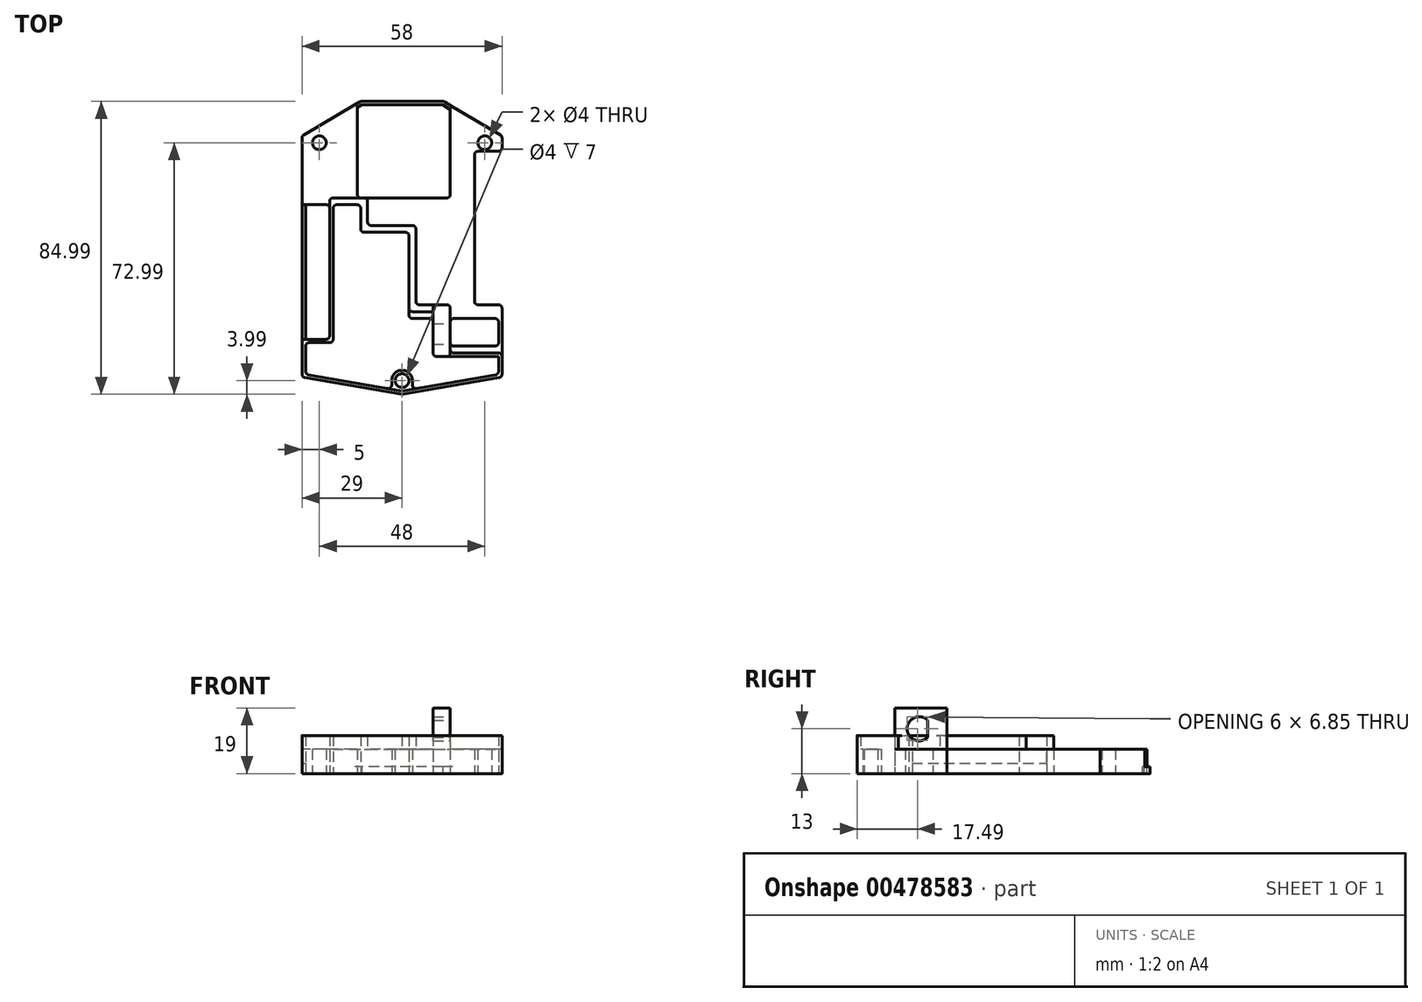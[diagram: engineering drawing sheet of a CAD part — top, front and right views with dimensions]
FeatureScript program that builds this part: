
annotation { "Feature Type Name" : "Feature", "Feature Type Description" : "" }
export const myFeature = defineFeature(function(context is Context, id is Id, definition is map)
    precondition{}
    {
        {
            var Q0;
            Q0=qCreatedBy(makeId("Top.planeOp"),FACE);
            var sketch = newSketch(context, id + "F0", { "sketchPlane" : qUnion([Q0])});
            skCircle(sketch, "E0", {"center": v(0, 0) * mm, "radius": 2 * mm});
            skLineSegment(sketch, "E1", {"start": v(0, 0) * mm, "end": v(0, -4) * mm, "construction": true});
            skLineSegment(sketch, "E2", {"start": v(0, -4) * mm, "end": v(-29, 1) * mm});
            skLineSegment(sketch, "E3.MirrorCS", {"start": v(0, -4) * mm, "end": v(29, 1) * mm});
            skLineSegment(sketch, "E4", {"start": v(-29, 1) * mm, "end": v(29, 1) * mm, "construction": true});
            skLineSegment(sketch, "E5", {"start": v(-29, 1) * mm, "end": v(-29, 71) * mm});
            skLineSegment(sketch, "E6", {"start": v(0, 0) * mm, "end": v(0, 81) * mm, "construction": true});
            skLineSegment(sketch, "E7.MirrorCS", {"start": v(29, 1) * mm, "end": v(29, 71) * mm});
            skLineSegment(sketch, "E8", {"start": v(12, 81) * mm, "end": v(-12, 81) * mm});
            skLineSegment(sketch, "E9", {"start": v(12, 81) * mm, "end": v(29, 71) * mm});
            skLineSegment(sketch, "E10", {"start": v(-12, 81) * mm, "end": v(-29, 71) * mm});
            skCircle(sketch, "E11", {"center": v(24, 69) * mm, "radius": 2 * mm});
            skCircle(sketch, "E12.MirrorC", {"center": v(-24, 69) * mm, "radius": 2 * mm});
            skSolve(sketch);
        }
        {
            var Q0;
            Q0=qCreatedBy(makeId("Top.planeOp"),FACE);
            var sketch = newSketch(context, id + "F1", { "sketchPlane" : qUnion([Q0])});
            skLineSegment(sketch, "E13.0.0", {"start": v(29, 71) * mm, "end": v(12, 81) * mm});
            skLineSegment(sketch, "E13.0.1", {"start": v(12, 81) * mm, "end": v(-12, 81) * mm});
            skLineSegment(sketch, "E13.0.2", {"start": v(-12, 81) * mm, "end": v(-29, 71) * mm});
            skLineSegment(sketch, "E13.0.3", {"start": v(-29, 71) * mm, "end": v(-29, 1) * mm});
            skLineSegment(sketch, "E13.0.4", {"start": v(-29, 1) * mm, "end": v(0, -4) * mm});
            skLineSegment(sketch, "E13.0.5", {"start": v(0, -4) * mm, "end": v(29, 1) * mm});
            skLineSegment(sketch, "E13.0.6", {"start": v(29, 1) * mm, "end": v(29, 22) * mm});
            skCircle(sketch, "E14.0", {"center": v(24, 69) * mm, "radius": 2 * mm});
            skCircle(sketch, "E15.0", {"center": v(-24, 69) * mm, "radius": 2 * mm});
            skCircle(sketch, "E16.0", {"center": v(0, 0) * mm, "radius": 2 * mm});
            skLineSegment(sketch, "E17", {"start": v(28, 18) * mm, "end": v(28, 1.84) * mm});
            skLineSegment(sketch, "E18", {"start": v(28, 1.84) * mm, "end": v(3, -2.47) * mm});
            skLineSegment(sketch, "E19", {"start": v(-3, -2.47) * mm, "end": v(-28, 1.84) * mm});
            skLineSegment(sketch, "E20", {"start": v(-28, 1.84) * mm, "end": v(-28, 51) * mm});
            skLineSegment(sketch, "E21", {"start": v(29, 22) * mm, "end": v(21, 22) * mm});
            skLineSegment(sketch, "E22", {"start": v(21, 22) * mm, "end": v(21, 66.5) * mm});
            skLineSegment(sketch, "E23", {"start": v(21, 66.5) * mm, "end": v(29, 66.5) * mm});
            skLineSegment(sketch, "E24", {"start": v(28, 18) * mm, "end": v(2, 18) * mm});
            skLineSegment(sketch, "E25", {"start": v(2, 18) * mm, "end": v(2, 43) * mm});
            skLineSegment(sketch, "E26", {"start": v(-12, 51) * mm, "end": v(-28, 51) * mm});
            skLineSegment(sketch, "E27", {"start": v(-12, 51) * mm, "end": v(-12, 43) * mm});
            skLineSegment(sketch, "E28", {"start": v(-12, 43) * mm, "end": v(2, 43) * mm});
            skArc(sketch, "E29", {"start": v(3, 0) * mm, "mid": v(0, 3) * mm, "end": v(-3, 0) * mm});
            skLineSegment(sketch, "E30", {"start": v(-3, 0) * mm, "end": v(-3, -2.47) * mm});
            skLineSegment(sketch, "E31", {"start": v(3, 0) * mm, "end": v(3, -2.47) * mm});
            skPoint(sketch, "E32", {"position": v(-28, 51) * mm});
            skPoint(sketch, "E33", {"position": v(28, 18) * mm});
            skPoint(sketch, "E34", {"position": v(28, 22) * mm});
            skPoint(sketch, "E35", {"position": v(28, 66.5) * mm});
            skPoint(sketch, "E36.orphan", {"position": v(-29, 51) * mm});
            skLineSegment(sketch, "E37.trimOffspring", {"start": v(29, 66.5) * mm, "end": v(29, 71) * mm});
            skPoint(sketch, "E38.orphan", {"position": v(0, -2.99) * mm});
            skLineSegment(sketch, "E39", {"start": v(-29, 11) * mm, "end": v(-20, 11) * mm});
            skLineSegment(sketch, "E40", {"start": v(-20, 11) * mm, "end": v(-20, 51) * mm});
            skLineSegment(sketch, "E41", {"start": v(-29, 12) * mm, "end": v(-21, 12) * mm});
            skLineSegment(sketch, "E42", {"start": v(-21, 12) * mm, "end": v(-21, 51) * mm});
            skLineSegment(sketch, "E43", {"start": v(-13, 80.41) * mm, "end": v(-13, 53) * mm});
            skLineSegment(sketch, "E44", {"start": v(-13, 53) * mm, "end": v(14, 53) * mm});
            skLineSegment(sketch, "E45", {"start": v(14, 53) * mm, "end": v(14, 79.82) * mm});
            skLineSegment(sketch, "E46", {"start": v(0, 81) * mm, "end": v(0, 53) * mm, "construction": true});
            skLineSegment(sketch, "E47", {"start": v(14, 78.66) * mm, "end": v(11.73, 80) * mm});
            skLineSegment(sketch, "E48", {"start": v(11.73, 80) * mm, "end": v(-11.73, 80) * mm});
            skLineSegment(sketch, "E49", {"start": v(-11.73, 80) * mm, "end": v(-13, 79.25) * mm});
            skLineSegment(sketch, "E50", {"start": v(28, 10) * mm, "end": v(14, 10) * mm});
            skLineSegment(sketch, "E51", {"start": v(14, 10) * mm, "end": v(14, 18) * mm});
            skLineSegment(sketch, "E52", {"start": v(9, 18) * mm, "end": v(9, 7) * mm});
            skLineSegment(sketch, "E53", {"start": v(9, 7) * mm, "end": v(28, 7) * mm});
            skSolve(sketch);
        }
        {
            var Q0;
            {var subQ0=sQuery(id+"F1.wireOp",EDGE,"E39");var subQ1=sQuery(id+"F1.wireOp",EDGE,"E13.0.3");var subQ2=makeQuery(id+"F1.imprint","INTERSECT",VERTEX,{"derivedFrom":[subQ1,subQ0]});Q0=makeQuery(id+"F1.imprint","IMPRINT",FACE,{"disambiguationData":[TD([[makeQuery(id+"F1.imprint","IMPRINT",EDGE,{"disambiguationData":[TD([[subQ2,1.0]])],"derivedFrom":subQ1}),1.0]])]});}
            var Q1;
            {var subQ0=sQuery(id+"F1.wireOp",EDGE,"E40");Q1=makeQuery(id+"F1.imprint","IMPRINT",FACE,{"disambiguationData":[TD([[makeQuery(id+"F1.imprint","IMPRINT",EDGE,{"derivedFrom":subQ0}),1.0]])]});}
            var Q2;
            {var subQ11=sQuery(id+"F1.wireOp",EDGE,"E13.0.4");Q2=makeQuery(id+"F1.imprint","IMPRINT",FACE,{"disambiguationData":[TD([[makeQuery(id+"F1.imprint","IMPRINT",EDGE,{"derivedFrom":subQ11}),1.0]])]});}
            var Q3;
            {var subQ1=sQuery(id+"F1.wireOp",EDGE,"E50");Q3=makeQuery(id+"F1.imprint","IMPRINT",FACE,{"disambiguationData":[TD([[makeQuery(id+"F1.imprint","IMPRINT",EDGE,{"derivedFrom":subQ1}),1.0]])]});}
            extrude(context, id + "F2", {"entities" : qUnion([Q0, Q1, Q2, Q3]), "depth" : 7 * mm, "offsetDistance" : 25 * mm});
        }
        {
            var Q0;
            Q0=makeQuery(id+"F2.opExtrude","CAP_FACE",FACE,{"disambiguationData":[OSD([sQuery(id+"F1.wireOp",EDGE,"E13.0.0"),sQuery(id+"F1.wireOp",EDGE,"E13.0.1"),sQuery(id+"F1.wireOp",EDGE,"E13.0.2"),sQuery(id+"F1.wireOp",EDGE,"E13.0.3"),sQuery(id+"F1.wireOp",EDGE,"E13.0.4"),sQuery(id+"F1.wireOp",EDGE,"E13.0.5"),sQuery(id+"F1.wireOp",EDGE,"E13.0.6"),sQuery(id+"F1.wireOp",EDGE,"E14.0"),sQuery(id+"F1.wireOp",EDGE,"E15.0"),sQuery(id+"F1.wireOp",EDGE,"E16.0"),sQuery(id+"F1.wireOp",EDGE,"E17"),sQuery(id+"F1.wireOp",EDGE,"E18"),sQuery(id+"F1.wireOp",EDGE,"E19"),sQuery(id+"F1.wireOp",EDGE,"E20"),sQuery(id+"F1.wireOp",EDGE,"E21"),sQuery(id+"F1.wireOp",EDGE,"E22"),sQuery(id+"F1.wireOp",EDGE,"E23"),sQuery(id+"F1.wireOp",EDGE,"E24"),sQuery(id+"F1.wireOp",EDGE,"E25"),sQuery(id+"F1.wireOp",EDGE,"E26"),sQuery(id+"F1.wireOp",EDGE,"E27"),sQuery(id+"F1.wireOp",EDGE,"E28"),sQuery(id+"F1.wireOp",EDGE,"E29"),sQuery(id+"F1.wireOp",EDGE,"E30"),sQuery(id+"F1.wireOp",EDGE,"E31"),sQuery(id+"F1.wireOp",EDGE,"E37.trimOffspring"),sQuery(id+"F1.wireOp",EDGE,"E39"),sQuery(id+"F1.wireOp",EDGE,"E40"),sQuery(id+"F1.wireOp",EDGE,"E41"),sQuery(id+"F1.wireOp",EDGE,"E42")])],"isStart":false});
            var sketch = newSketch(context, id + "F3", { "sketchPlane" : qUnion([Q0])});
            skLineSegment(sketch, "E54", {"start": v(21, 22) * mm, "end": v(21, 33) * mm});
            skLineSegment(sketch, "E55", {"start": v(4, 33) * mm, "end": v(4, 45) * mm});
            skLineSegment(sketch, "E56", {"start": v(4, 45) * mm, "end": v(-10, 45) * mm});
            skLineSegment(sketch, "E57", {"start": v(-10, 45) * mm, "end": v(-10, 53) * mm});
            skLineSegment(sketch, "E58", {"start": v(-10, 53) * mm, "end": v(-21, 53) * mm});
            skLineSegment(sketch, "E59", {"start": v(-21, 53) * mm, "end": v(-21, 51) * mm});
            skLineSegment(sketch, "E60.0", {"start": v(-21, 12) * mm, "end": v(-21, 51) * mm});
            skLineSegment(sketch, "E61.0", {"start": v(-28, 12) * mm, "end": v(-21, 12) * mm});
            skLineSegment(sketch, "E62.0", {"start": v(-28, 11) * mm, "end": v(-20, 11) * mm});
            skLineSegment(sketch, "E63.0", {"start": v(-20, 11) * mm, "end": v(-20, 51) * mm});
            skLineSegment(sketch, "E64", {"start": v(-20, 51) * mm, "end": v(-12, 51) * mm});
            skLineSegment(sketch, "E65.0", {"start": v(-12, 51) * mm, "end": v(-12, 43) * mm});
            skLineSegment(sketch, "E66.0", {"start": v(-12, 43) * mm, "end": v(2, 43) * mm});
            skLineSegment(sketch, "E67", {"start": v(2, 33) * mm, "end": v(2, 43) * mm});
            skLineSegment(sketch, "E68", {"start": v(-28, 12) * mm, "end": v(-29, 12) * mm});
            skLineSegment(sketch, "E69", {"start": v(-29, 12) * mm, "end": v(-29, 1) * mm});
            skLineSegment(sketch, "E70", {"start": v(-29, 1) * mm, "end": v(-3.17, -3.45) * mm});
            skLineSegment(sketch, "E71", {"start": v(-3.17, -3.45) * mm, "end": v(-3, -2.47) * mm});
            skLineSegment(sketch, "E72", {"start": v(-3, -2.47) * mm, "end": v(-28, 1.84) * mm});
            skLineSegment(sketch, "E73", {"start": v(-28, 1.84) * mm, "end": v(-28, 11) * mm});
            skLineSegment(sketch, "E74.0", {"start": v(29, 22) * mm, "end": v(21, 22) * mm});
            skLineSegment(sketch, "E75.0", {"start": v(28, 1.84) * mm, "end": v(3, -2.47) * mm});
            skLineSegment(sketch, "E76.0", {"start": v(-29, 1) * mm, "end": v(0, -4) * mm});
            skLineSegment(sketch, "E77.0", {"start": v(0, -4) * mm, "end": v(29, 1) * mm});
            skLineSegment(sketch, "E78.0", {"start": v(29, 1) * mm, "end": v(29, 8) * mm});
            skLineSegment(sketch, "E79", {"start": v(-3, -2.47) * mm, "end": v(0, -2.99) * mm});
            skLineSegment(sketch, "E80", {"start": v(0, -2.99) * mm, "end": v(3, -2.47) * mm});
            skLineSegment(sketch, "E81", {"start": v(2, 31) * mm, "end": v(2, 33) * mm});
            skLineSegment(sketch, "E82", {"start": v(9, 20) * mm, "end": v(2, 20) * mm});
            skLineSegment(sketch, "E83", {"start": v(2, 20) * mm, "end": v(2, 31) * mm});
            skLineSegment(sketch, "E84", {"start": v(4, 33) * mm, "end": v(4, 22) * mm});
            skLineSegment(sketch, "E85", {"start": v(4, 22) * mm, "end": v(21, 22) * mm});
            skLineSegment(sketch, "E86.0", {"start": v(9, 18) * mm, "end": v(9, 7) * mm});
            skLineSegment(sketch, "E87.0", {"start": v(14, 10) * mm, "end": v(14, 18) * mm});
            skLineSegment(sketch, "E88", {"start": v(9, 18) * mm, "end": v(9, 20) * mm});
            skLineSegment(sketch, "E89", {"start": v(14, 18) * mm, "end": v(14, 20) * mm});
            skLineSegment(sketch, "E90", {"start": v(14, 10) * mm, "end": v(14, 8) * mm});
            skLineSegment(sketch, "E91", {"start": v(14, 8) * mm, "end": v(29, 8) * mm});
            skLineSegment(sketch, "E92.0", {"start": v(9, 7) * mm, "end": v(28, 7) * mm});
            skLineSegment(sketch, "E93.0", {"start": v(28, 7) * mm, "end": v(28, 1.84) * mm});
            skLineSegment(sketch, "E94", {"start": v(14, 20) * mm, "end": v(14, 22) * mm});
            skSolve(sketch);
        }
        {
            var Q0;
            Q0 = qSketchRegion(id + "F3", true);
            extrude(context, id + "F4", {"entities" : qUnion([Q0]), "operationType" : NewBodyOperationType.ADD, "depth" : 4 * mm, "offsetDistance" : 25 * mm});
        }
        {
            var Q0;
            Q0=makeQuery(id+"F4.opExtrude","CAP_FACE",FACE,{"disambiguationData":[OSD([sQuery(id+"F3.wireOp",EDGE,"E55"),sQuery(id+"F3.wireOp",EDGE,"E56"),sQuery(id+"F3.wireOp",EDGE,"E57"),sQuery(id+"F3.wireOp",EDGE,"E58"),sQuery(id+"F3.wireOp",EDGE,"E59"),sQuery(id+"F3.wireOp",EDGE,"E60.0"),sQuery(id+"F3.wireOp",EDGE,"E61.0"),sQuery(id+"F3.wireOp",EDGE,"E62.0"),sQuery(id+"F3.wireOp",EDGE,"E63.0"),sQuery(id+"F3.wireOp",EDGE,"E64"),sQuery(id+"F3.wireOp",EDGE,"E65.0"),sQuery(id+"F3.wireOp",EDGE,"E66.0"),sQuery(id+"F3.wireOp",EDGE,"E67"),sQuery(id+"F3.wireOp",EDGE,"E68"),sQuery(id+"F3.wireOp",EDGE,"E69"),sQuery(id+"F3.wireOp",EDGE,"E72"),sQuery(id+"F3.wireOp",EDGE,"E73"),sQuery(id+"F3.wireOp",EDGE,"E75.0"),sQuery(id+"F3.wireOp",EDGE,"E76.0"),sQuery(id+"F3.wireOp",EDGE,"E77.0"),sQuery(id+"F3.wireOp",EDGE,"E78.0"),sQuery(id+"F3.wireOp",EDGE,"E79"),sQuery(id+"F3.wireOp",EDGE,"E80"),sQuery(id+"F3.wireOp",EDGE,"E81"),sQuery(id+"F3.wireOp",EDGE,"E82"),sQuery(id+"F3.wireOp",EDGE,"E83"),sQuery(id+"F3.wireOp",EDGE,"E84"),sQuery(id+"F3.wireOp",EDGE,"E85"),sQuery(id+"F3.wireOp",EDGE,"E86.0"),sQuery(id+"F3.wireOp",EDGE,"E87.0"),sQuery(id+"F3.wireOp",EDGE,"E88"),sQuery(id+"F3.wireOp",EDGE,"E89"),sQuery(id+"F3.wireOp",EDGE,"E90"),sQuery(id+"F3.wireOp",EDGE,"E91"),sQuery(id+"F3.wireOp",EDGE,"E92.0"),sQuery(id+"F3.wireOp",EDGE,"E93.0"),sQuery(id+"F3.wireOp",EDGE,"E94")])],"isStart":false});
            var sketch = newSketch(context, id + "F5", { "sketchPlane" : qUnion([Q0])});
            skLineSegment(sketch, "E95.0", {"start": v(9, 7) * mm, "end": v(9, 20) * mm});
            skLineSegment(sketch, "E96.0", {"start": v(14, 22) * mm, "end": v(14, 8) * mm});
            skLineSegment(sketch, "E97", {"start": v(9, 7) * mm, "end": v(14, 7) * mm});
            skLineSegment(sketch, "E98", {"start": v(14, 7) * mm, "end": v(14, 8) * mm});
            skLineSegment(sketch, "E99", {"start": v(14, 22) * mm, "end": v(9, 22) * mm});
            skLineSegment(sketch, "E100", {"start": v(9, 22) * mm, "end": v(9, 20) * mm});
            skSolve(sketch);
        }
        {
            var Q0;
            Q0 = qSketchRegion(id + "F5", true);
            extrude(context, id + "F6", {"entities" : qUnion([Q0]), "operationType" : NewBodyOperationType.ADD, "depth" : 8 * mm, "offsetDistance" : 25 * mm});
        }
        {
            var Q0;
            Q0=makeQuery(id+"F4.boolean.opBoolean","MERGE",FACE,{"derivedFrom":[makeQuery(id+"F2.opExtrude","SWEPT_FACE",FACE,{"disambiguationData":[OSD([sQuery(id+"F1.wireOp",EDGE,"E13.0.6")])]}),makeQuery(id+"F4.opExtrude","SWEPT_FACE",FACE,{"disambiguationData":[OSD([sQuery(id+"F3.wireOp",EDGE,"E78.0")])]})]});
            var sketch = newSketch(context, id + "F7", { "sketchPlane" : qUnion([Q0])});
            skCircle(sketch, "E101", {"center": v(14, 13) * mm, "radius": 3.5 * mm});
            skLineSegment(sketch, "E102", {"start": v(14, 13) * mm, "end": v(14, 11) * mm, "construction": true});
            skLineSegment(sketch, "E103", {"start": v(14, 13) * mm, "end": v(14, 0) * mm, "construction": true});
            skLineSegment(sketch, "E104", {"start": v(16.5, 15.45) * mm, "end": v(16.5, 10.55) * mm});
            skLineSegment(sketch, "E105", {"start": v(14, 13) * mm, "end": v(10.5, 13) * mm, "construction": true});
            skPoint(sketch, "E106.0", {"position": v(1, 0) * mm});
            skSolve(sketch);
        }
        {
            var Q0;
            {var subQ0=sQuery(id+"F7.wireOp",EDGE,"E104");Q0=makeQuery(id+"F7.imprint","IMPRINT",FACE,{"disambiguationData":[TD([[makeQuery(id+"F7.imprint","IMPRINT",EDGE,{"derivedFrom":subQ0}),-1.0]])]});}
            extrude(context, id + "F8", {"entities" : qUnion([Q0]), "operationType" : NewBodyOperationType.REMOVE, "oppositeDirection" : true, "depth" : 25 * mm, "offsetDistance" : 25 * mm});
        }
        {
            var Q0;
            {var subQ0=sQuery(id+"F1.wireOp",EDGE,"E45");var subQ1=sQuery(id+"F1.wireOp",EDGE,"E44");var subQ2=sQuery(id+"F1.wireOp",EDGE,"E43");var subQ3=sQuery(id+"F1.wireOp",EDGE,"E37.trimOffspring");var subQ4=sQuery(id+"F1.wireOp",EDGE,"E13.0.3");var subQ5=sQuery(id+"F1.wireOp",EDGE,"E26");var subQ6=sQuery(id+"F1.wireOp",EDGE,"E20");var subQ8=sQuery(id+"F1.wireOp",EDGE,"E41");var subQ9=sQuery(id+"F1.wireOp",EDGE,"E14.0");var subQ10=sQuery(id+"F1.wireOp",EDGE,"E13.0.2");var subQ11=sQuery(id+"F1.wireOp",EDGE,"E13.0.0");var subQ12=sQuery(id+"F1.wireOp",EDGE,"E42");var subQ13=sQuery(id+"F1.wireOp",EDGE,"E15.0");var subQ14=sQuery(id+"F1.wireOp",EDGE,"E22");var subQ15=sQuery(id+"F1.wireOp",EDGE,"E23");Q0=makeQuery(id+"F4.boolean.opBoolean","SPLIT",FACE,{"disambiguationData":[TD([makeQuery(id+"F2.opExtrude","SWEPT_FACE",FACE,{"disambiguationData":[OSD([subQ11])]})])],"derivedFrom":makeQuery(id+"F2.opExtrude","CAP_FACE",FACE,{"disambiguationData":[OSD([subQ11,subQ10,subQ4,sQuery(id+"F1.wireOp",EDGE,"E13.0.4"),sQuery(id+"F1.wireOp",EDGE,"E13.0.5"),sQuery(id+"F1.wireOp",EDGE,"E13.0.6"),subQ9,subQ13,sQuery(id+"F1.wireOp",EDGE,"E16.0"),sQuery(id+"F1.wireOp",EDGE,"E17"),sQuery(id+"F1.wireOp",EDGE,"E18"),sQuery(id+"F1.wireOp",EDGE,"E19"),subQ6,sQuery(id+"F1.wireOp",EDGE,"E21"),subQ14,subQ15,sQuery(id+"F1.wireOp",EDGE,"E24"),sQuery(id+"F1.wireOp",EDGE,"E25"),subQ5,sQuery(id+"F1.wireOp",EDGE,"E27"),sQuery(id+"F1.wireOp",EDGE,"E28"),sQuery(id+"F1.wireOp",EDGE,"E29"),sQuery(id+"F1.wireOp",EDGE,"E30"),sQuery(id+"F1.wireOp",EDGE,"E31"),subQ3,sQuery(id+"F1.wireOp",EDGE,"E39"),sQuery(id+"F1.wireOp",EDGE,"E40"),subQ8,subQ12,subQ2,subQ1,subQ0])],"isStart":false})});}
            var sketch = newSketch(context, id + "F9", { "sketchPlane" : qUnion([Q0])});
            skLineSegment(sketch, "E107.0", {"start": v(-29, 12) * mm, "end": v(-28, 12) * mm});
            skLineSegment(sketch, "E108.0", {"start": v(-28, 12) * mm, "end": v(-28, 51) * mm});
            skLineSegment(sketch, "E109.0", {"start": v(-29, 51) * mm, "end": v(-29, 12) * mm});
            skLineSegment(sketch, "E110", {"start": v(-28, 51) * mm, "end": v(-29, 51) * mm});
            skPoint(sketch, "E111.orphan", {"position": v(-29, 71) * mm});
            skSolve(sketch);
        }
        {
            var Q0;
            Q0 = qSketchRegion(id + "F9", true);
            extrude(context, id + "F10", {"entities" : qUnion([Q0]), "operationType" : NewBodyOperationType.REMOVE, "oppositeDirection" : true, "depth" : 4 * mm, "offsetDistance" : 25 * mm});
        }
        {
            var Q0;
            {var subQ4=sQuery(id+"F1.wireOp",EDGE,"E13.0.1");Q0=makeQuery(id+"F1.imprint","IMPRINT",FACE,{"disambiguationData":[TD([[makeQuery(id+"F1.imprint","IMPRINT",EDGE,{"derivedFrom":subQ4}),1.0]])]});}
            extrude(context, id + "F11", {"entities" : qUnion([Q0]), "operationType" : NewBodyOperationType.ADD, "depth" : 2 * mm, "offsetDistance" : 25 * mm});
        }
        {
            var Q0;
            Q0=makeQuery(id+"F2.opExtrude","SWEPT_EDGE",EDGE,{"disambiguationData":[OSD([sQuery(id+"F1.wireOp",EDGE,"E13.0.0"),sQuery(id+"F1.wireOp",EDGE,"E37.trimOffspring")])]});
            var Q1;
            Q1=makeQuery(id+"F2.opExtrude","SWEPT_EDGE",EDGE,{"disambiguationData":[OSD([sQuery(id+"F1.wireOp",EDGE,"E13.0.2"),sQuery(id+"F1.wireOp",EDGE,"E13.0.3")])]});
            var Q2;
            Q2=makeQuery(id+"F2.opExtrude","SWEPT_EDGE",EDGE,{"disambiguationData":[OSD([sQuery(id+"F1.wireOp",EDGE,"E43"),sQuery(id+"F1.wireOp",EDGE,"E44")])]});
            var Q3;
            Q3=makeQuery(id+"F2.opExtrude","SWEPT_EDGE",EDGE,{"disambiguationData":[OSD([sQuery(id+"F1.wireOp",EDGE,"E44"),sQuery(id+"F1.wireOp",EDGE,"E45")])]});
            var Q4;
            Q4=makeQuery(id+"F4.opExtrude","SWEPT_EDGE",EDGE,{"disambiguationData":[OSD([sQuery(id+"F3.wireOp",EDGE,"E55"),sQuery(id+"F3.wireOp",EDGE,"E56")])]});
            var Q5;
            Q5=makeQuery(id+"F4.opExtrude","SWEPT_EDGE",EDGE,{"disambiguationData":[OSD([sQuery(id+"F3.wireOp",EDGE,"E56"),sQuery(id+"F3.wireOp",EDGE,"E57")])]});
            var Q6;
            Q6=makeQuery(id+"F4.opExtrude","SWEPT_EDGE",EDGE,{"disambiguationData":[OSD([sQuery(id+"F3.wireOp",EDGE,"E57"),sQuery(id+"F3.wireOp",EDGE,"E58")])]});
            var Q7;
            Q7=makeQuery(id+"F4.opExtrude","SWEPT_EDGE",EDGE,{"disambiguationData":[OSD([sQuery(id+"F3.wireOp",EDGE,"E58"),sQuery(id+"F3.wireOp",EDGE,"E59")])]});
            var Q8;
            Q8=makeQuery(id+"F4.opExtrude","SWEPT_EDGE",EDGE,{"disambiguationData":[OSD([sQuery(id+"F3.wireOp",EDGE,"ofNKhmwy-Z57V-YwXv-PZbO-5RSoCvZKl6zs"),sQuery(id+"F3.wireOp",EDGE,"E55")])]});
            var Q9;
            Q9=makeQuery(id+"F4.opExtrude","SWEPT_EDGE",EDGE,{"disambiguationData":[OSD([sQuery(id+"F1.wireOp",EDGE,"E22"),sQuery(id+"F3.wireOp",EDGE,"E54"),sQuery(id+"F3.wireOp",EDGE,"ofNKhmwy-Z57V-YwXv-PZbO-5RSoCvZKl6zs")])]});
            var Q10;
            Q10=makeQuery(id+"F4.boolean.opBoolean","MERGE",EDGE,{"derivedFrom":[makeQuery(id+"F2.opExtrude","SWEPT_EDGE",EDGE,{"disambiguationData":[OSD([sQuery(id+"F1.wireOp",EDGE,"E21"),sQuery(id+"F1.wireOp",EDGE,"E22")])]}),makeQuery(id+"F4.opExtrude","SWEPT_EDGE",EDGE,{"disambiguationData":[OSD([sQuery(id+"F3.wireOp",EDGE,"E54"),sQuery(id+"F3.wireOp",EDGE,"E74.0")])]})]});
            var Q11;
            Q11=makeQuery(id+"F4.boolean.opBoolean","MERGE",EDGE,{"derivedFrom":[makeQuery(id+"F2.opExtrude","SWEPT_EDGE",EDGE,{"disambiguationData":[OSD([sQuery(id+"F1.wireOp",EDGE,"E13.0.6"),sQuery(id+"F1.wireOp",EDGE,"E21")])]}),makeQuery(id+"F4.opExtrude","SWEPT_EDGE",EDGE,{"disambiguationData":[OSD([sQuery(id+"F3.wireOp",EDGE,"E74.0"),sQuery(id+"F3.wireOp",EDGE,"E78.0")])]})]});
            var Q12;
            Q12=makeQuery(id+"F4.boolean.opBoolean","MERGE",EDGE,{"derivedFrom":[makeQuery(id+"F2.opExtrude","SWEPT_EDGE",EDGE,{"disambiguationData":[OSD([sQuery(id+"F1.wireOp",EDGE,"E13.0.5"),sQuery(id+"F1.wireOp",EDGE,"E13.0.6")])]}),makeQuery(id+"F4.opExtrude","SWEPT_EDGE",EDGE,{"disambiguationData":[OSD([sQuery(id+"F3.wireOp",EDGE,"E77.0"),sQuery(id+"F3.wireOp",EDGE,"E78.0")])]})]});
            var Q13;
            Q13=makeQuery(id+"F4.boolean.opBoolean","MERGE",EDGE,{"derivedFrom":[makeQuery(id+"F2.opExtrude","SWEPT_EDGE",EDGE,{"disambiguationData":[OSD([sQuery(id+"F1.wireOp",EDGE,"E13.0.3"),sQuery(id+"F1.wireOp",EDGE,"E13.0.4")])]}),makeQuery(id+"F4.opExtrude","SWEPT_EDGE",EDGE,{"disambiguationData":[OSD([sQuery(id+"F3.wireOp",EDGE,"E69"),sQuery(id+"F3.wireOp",EDGE,"E76.0")])]})]});
            var Q14;
            Q14=makeQuery(id+"F4.opExtrude","SWEPT_EDGE",EDGE,{"disambiguationData":[OSD([sQuery(id+"F1.wireOp",EDGE,"E13.0.3"),sQuery(id+"F3.wireOp",EDGE,"E68"),sQuery(id+"F3.wireOp",EDGE,"E69")])]});
            var Q15;
            Q15=makeQuery(id+"F4.boolean.opBoolean","MERGE",EDGE,{"derivedFrom":[makeQuery(id+"F2.opExtrude","SWEPT_EDGE",EDGE,{"disambiguationData":[OSD([sQuery(id+"F1.wireOp",EDGE,"E41"),sQuery(id+"F1.wireOp",EDGE,"E42")])]}),makeQuery(id+"F4.opExtrude","SWEPT_EDGE",EDGE,{"disambiguationData":[OSD([sQuery(id+"F3.wireOp",EDGE,"E60.0"),sQuery(id+"F3.wireOp",EDGE,"E61.0")])]})]});
            var Q16;
            Q16=makeQuery(id+"F4.boolean.opBoolean","MERGE",EDGE,{"derivedFrom":[makeQuery(id+"F2.opExtrude","SWEPT_EDGE",EDGE,{"disambiguationData":[OSD([sQuery(id+"F1.wireOp",EDGE,"E13.0.4"),sQuery(id+"F1.wireOp",EDGE,"E13.0.5")])]}),makeQuery(id+"F4.opExtrude","SWEPT_EDGE",EDGE,{"disambiguationData":[OSD([sQuery(id+"F3.wireOp",EDGE,"E76.0"),sQuery(id+"F3.wireOp",EDGE,"E77.0")])]})]});
            var Q17;
            Q17=makeQuery(id+"F2.opExtrude","SWEPT_EDGE",EDGE,{"disambiguationData":[OSD([sQuery(id+"F1.wireOp",EDGE,"E22"),sQuery(id+"F1.wireOp",EDGE,"E23")])]});
            var Q18;
            Q18=makeQuery(id+"F2.opExtrude","SWEPT_EDGE",EDGE,{"disambiguationData":[OSD([sQuery(id+"F1.wireOp",EDGE,"E23"),sQuery(id+"F1.wireOp",EDGE,"E37.trimOffspring")])]});
            var Q19;
            Q19=makeQuery(id+"F10.boolean.opBoolean","COPY",EDGE,{"derivedFrom":makeQuery(id+"F10.opExtrude","SWEPT_EDGE",EDGE,{"disambiguationData":[OSD([sQuery(id+"F9.wireOp",EDGE,"E109.0"),sQuery(id+"F9.wireOp",EDGE,"E110")])]})});
            var Q20;
            Q20=makeQuery(id+"F2.opExtrude","SWEPT_EDGE",EDGE,{"disambiguationData":[OSD([sQuery(id+"F1.wireOp",EDGE,"E26"),sQuery(id+"F1.wireOp",EDGE,"E42")])]});
            var Q21;
            Q21=makeQuery(id+"F11.opExtrude","SWEPT_EDGE",EDGE,{"disambiguationData":[OSD([sQuery(id+"F1.wireOp",EDGE,"E43"),sQuery(id+"F1.wireOp",EDGE,"E49")])]});
            var Q22;
            Q22=makeQuery(id+"F11.opExtrude","SWEPT_EDGE",EDGE,{"disambiguationData":[OSD([sQuery(id+"F1.wireOp",EDGE,"E13.0.1"),sQuery(id+"F1.wireOp",EDGE,"E13.0.2")])]});
            var Q23;
            Q23=makeQuery(id+"F11.opExtrude","SWEPT_EDGE",EDGE,{"disambiguationData":[OSD([sQuery(id+"F1.wireOp",EDGE,"E13.0.0"),sQuery(id+"F1.wireOp",EDGE,"E13.0.1")])]});
            var Q24;
            Q24=makeQuery(id+"F11.opExtrude","SWEPT_EDGE",EDGE,{"disambiguationData":[OSD([sQuery(id+"F1.wireOp",EDGE,"E45"),sQuery(id+"F1.wireOp",EDGE,"E47")])]});
            var Q25;
            Q25=makeQuery(id+"F4.boolean.opBoolean","MERGE",EDGE,{"derivedFrom":[makeQuery(id+"F2.opExtrude","SWEPT_EDGE",EDGE,{"disambiguationData":[OSD([sQuery(id+"F1.wireOp",EDGE,"E27"),sQuery(id+"F1.wireOp",EDGE,"E28")])]}),makeQuery(id+"F4.opExtrude","SWEPT_EDGE",EDGE,{"disambiguationData":[OSD([sQuery(id+"F3.wireOp",EDGE,"E65.0"),sQuery(id+"F3.wireOp",EDGE,"E66.0")])]})]});
            var Q26;
            Q26=makeQuery(id+"F4.boolean.opBoolean","MERGE",EDGE,{"derivedFrom":[makeQuery(id+"F2.opExtrude","SWEPT_EDGE",EDGE,{"disambiguationData":[OSD([sQuery(id+"F1.wireOp",EDGE,"E25"),sQuery(id+"F1.wireOp",EDGE,"E28")])]}),makeQuery(id+"F4.opExtrude","SWEPT_EDGE",EDGE,{"disambiguationData":[OSD([sQuery(id+"F3.wireOp",EDGE,"E66.0"),sQuery(id+"F3.wireOp",EDGE,"E67")])]})]});
            var Q27;
            Q27=makeQuery(id+"F4.boolean.opBoolean","MERGE",EDGE,{"derivedFrom":[makeQuery(id+"F2.opExtrude","SWEPT_EDGE",EDGE,{"disambiguationData":[OSD([sQuery(id+"F1.wireOp",EDGE,"E26"),sQuery(id+"F1.wireOp",EDGE,"E27")])]}),makeQuery(id+"F4.opExtrude","SWEPT_EDGE",EDGE,{"disambiguationData":[OSD([sQuery(id+"F3.wireOp",EDGE,"E64"),sQuery(id+"F3.wireOp",EDGE,"E65.0")])]})]});
            var Q28;
            Q28=makeQuery(id+"F4.boolean.opBoolean","MERGE",EDGE,{"derivedFrom":[makeQuery(id+"F2.opExtrude","SWEPT_EDGE",EDGE,{"disambiguationData":[OSD([sQuery(id+"F1.wireOp",EDGE,"E26"),sQuery(id+"F1.wireOp",EDGE,"E40")])]}),makeQuery(id+"F4.opExtrude","SWEPT_EDGE",EDGE,{"disambiguationData":[OSD([sQuery(id+"F3.wireOp",EDGE,"E63.0"),sQuery(id+"F3.wireOp",EDGE,"E64")])]})]});
            var Q29;
            Q29=makeQuery(id+"F4.boolean.opBoolean","MERGE",EDGE,{"derivedFrom":[makeQuery(id+"F2.opExtrude","SWEPT_EDGE",EDGE,{"disambiguationData":[OSD([sQuery(id+"F1.wireOp",EDGE,"E39"),sQuery(id+"F1.wireOp",EDGE,"E40")])]}),makeQuery(id+"F4.opExtrude","SWEPT_EDGE",EDGE,{"disambiguationData":[OSD([sQuery(id+"F3.wireOp",EDGE,"E62.0"),sQuery(id+"F3.wireOp",EDGE,"E63.0")])]})]});
            var Q30;
            Q30=makeQuery(id+"F4.boolean.opBoolean","MERGE",EDGE,{"derivedFrom":[makeQuery(id+"F2.opExtrude","SWEPT_EDGE",EDGE,{"disambiguationData":[OSD([sQuery(id+"F1.wireOp",EDGE,"E20"),sQuery(id+"F1.wireOp",EDGE,"E39")])]}),makeQuery(id+"F4.opExtrude","SWEPT_EDGE",EDGE,{"disambiguationData":[OSD([sQuery(id+"F3.wireOp",EDGE,"E62.0"),sQuery(id+"F3.wireOp",EDGE,"E73")])]})]});
            var Q31;
            Q31=makeQuery(id+"F4.boolean.opBoolean","MERGE",EDGE,{"derivedFrom":[makeQuery(id+"F2.opExtrude","SWEPT_EDGE",EDGE,{"disambiguationData":[OSD([sQuery(id+"F1.wireOp",EDGE,"E19"),sQuery(id+"F1.wireOp",EDGE,"E20")])]}),makeQuery(id+"F4.opExtrude","SWEPT_EDGE",EDGE,{"disambiguationData":[OSD([sQuery(id+"F3.wireOp",EDGE,"E72"),sQuery(id+"F3.wireOp",EDGE,"E73")])]})]});
            var Q32;
            Q32=makeQuery(id+"F4.opExtrude","SWEPT_EDGE",EDGE,{"disambiguationData":[OSD([sQuery(id+"F3.wireOp",EDGE,"E84"),sQuery(id+"F3.wireOp",EDGE,"E85")])]});
            var Q33;
            Q33=makeQuery(id+"F6.boolean.opBoolean","MERGE",EDGE,{"derivedFrom":[makeQuery(id+"F4.opExtrude","SWEPT_EDGE",EDGE,{"disambiguationData":[OSD([sQuery(id+"F3.wireOp",EDGE,"E85"),sQuery(id+"F3.wireOp",EDGE,"E94")])]}),makeQuery(id+"F6.opExtrude","SWEPT_EDGE",EDGE,{"disambiguationData":[OSD([sQuery(id+"F5.wireOp",EDGE,"E96.0"),sQuery(id+"F5.wireOp",EDGE,"E99")])]})]});
            var Q34;
            Q34=makeQuery(id+"F6.opExtrude","SWEPT_EDGE",EDGE,{"disambiguationData":[OSD([sQuery(id+"F3.wireOp",EDGE,"E85"),sQuery(id+"F5.wireOp",EDGE,"E99"),sQuery(id+"F5.wireOp",EDGE,"E100")])]});
            var Q35;
            Q35=makeQuery(id+"F2.opExtrude","SWEPT_EDGE",EDGE,{"disambiguationData":[OSD([sQuery(id+"F1.wireOp",EDGE,"E21"),sQuery(id+"F1.wireOp",EDGE,"E22")])]});
            var Q36;
            Q36=makeQuery(id+"F2.opExtrude","SWEPT_EDGE",EDGE,{"disambiguationData":[OSD([sQuery(id+"F1.wireOp",EDGE,"E13.0.6"),sQuery(id+"F1.wireOp",EDGE,"E21")])]});
            var Q37;
            Q37=makeQuery(id+"F6.opExtrude","SWEPT_EDGE",EDGE,{"disambiguationData":[OSD([sQuery(id+"F3.wireOp",EDGE,"E92.0"),sQuery(id+"F5.wireOp",EDGE,"E97"),sQuery(id+"F5.wireOp",EDGE,"E98")])]});
            var Q38;
            Q38=makeQuery(id+"F4.opExtrude","SWEPT_EDGE",EDGE,{"disambiguationData":[OSD([sQuery(id+"F3.wireOp",EDGE,"E90"),sQuery(id+"F3.wireOp",EDGE,"E91")])]});
            var Q39;
            Q39=makeQuery(id+"F2.opExtrude","SWEPT_EDGE",EDGE,{"disambiguationData":[OSD([sQuery(id+"F1.wireOp",EDGE,"E50"),sQuery(id+"F1.wireOp",EDGE,"E51")])]});
            var Q40;
            Q40=makeQuery(id+"F2.opExtrude","SWEPT_EDGE",EDGE,{"disambiguationData":[OSD([sQuery(id+"F1.wireOp",EDGE,"E24"),sQuery(id+"F1.wireOp",EDGE,"E51")])]});
            var Q41;
            Q41=makeQuery(id+"F2.opExtrude","SWEPT_EDGE",EDGE,{"disambiguationData":[OSD([sQuery(id+"F1.wireOp",EDGE,"E17"),sQuery(id+"F1.wireOp",EDGE,"E24")])]});
            var Q42;
            Q42=makeQuery(id+"F6.boolean.opBoolean","MERGE",EDGE,{"derivedFrom":[makeQuery(id+"F4.boolean.opBoolean","MERGE",EDGE,{"derivedFrom":[makeQuery(id+"F2.opExtrude","SWEPT_EDGE",EDGE,{"disambiguationData":[OSD([sQuery(id+"F1.wireOp",EDGE,"E52"),sQuery(id+"F1.wireOp",EDGE,"E53")])]}),makeQuery(id+"F4.opExtrude","SWEPT_EDGE",EDGE,{"disambiguationData":[OSD([sQuery(id+"F3.wireOp",EDGE,"E86.0"),sQuery(id+"F3.wireOp",EDGE,"E92.0")])]})]}),makeQuery(id+"F6.opExtrude","SWEPT_EDGE",EDGE,{"disambiguationData":[OSD([sQuery(id+"F5.wireOp",EDGE,"E95.0"),sQuery(id+"F5.wireOp",EDGE,"E97")])]})]});
            var Q43;
            Q43=makeQuery(id+"F2.opExtrude","SWEPT_EDGE",EDGE,{"disambiguationData":[OSD([sQuery(id+"F1.wireOp",EDGE,"E24"),sQuery(id+"F1.wireOp",EDGE,"E52")])]});
            var Q44;
            Q44=makeQuery(id+"F2.opExtrude","SWEPT_EDGE",EDGE,{"disambiguationData":[OSD([sQuery(id+"F1.wireOp",EDGE,"E24"),sQuery(id+"F1.wireOp",EDGE,"E25")])]});
            var Q45;
            Q45=makeQuery(id+"F4.opExtrude","SWEPT_EDGE",EDGE,{"disambiguationData":[OSD([sQuery(id+"F3.wireOp",EDGE,"E82"),sQuery(id+"F3.wireOp",EDGE,"E88")])]});
            var Q46;
            Q46=makeQuery(id+"F4.opExtrude","SWEPT_EDGE",EDGE,{"disambiguationData":[OSD([sQuery(id+"F1.wireOp",EDGE,"E25"),sQuery(id+"F3.wireOp",EDGE,"E82"),sQuery(id+"F3.wireOp",EDGE,"E83")])]});
            var Q47;
            Q47=makeQuery(id+"F4.opExtrude","SWEPT_EDGE",EDGE,{"disambiguationData":[OSD([sQuery(id+"F1.wireOp",EDGE,"E13.0.6"),sQuery(id+"F3.wireOp",EDGE,"E78.0"),sQuery(id+"F3.wireOp",EDGE,"E91")])]});
            var Q48;
            Q48=makeQuery(id+"F2.opExtrude","SWEPT_EDGE",EDGE,{"disambiguationData":[OSD([sQuery(id+"F1.wireOp",EDGE,"E17"),sQuery(id+"F1.wireOp",EDGE,"E50")])]});
            var Q49;
            Q49=makeQuery(id+"F2.opExtrude","SWEPT_EDGE",EDGE,{"disambiguationData":[OSD([sQuery(id+"F1.wireOp",EDGE,"E19"),sQuery(id+"F1.wireOp",EDGE,"E30")])]});
            var Q50;
            Q50=makeQuery(id+"F2.opExtrude","SWEPT_EDGE",EDGE,{"disambiguationData":[OSD([sQuery(id+"F1.wireOp",EDGE,"E18"),sQuery(id+"F1.wireOp",EDGE,"E31")])]});
            var Q51;
            Q51=makeQuery(id+"F4.boolean.opBoolean","MERGE",EDGE,{"derivedFrom":[makeQuery(id+"F2.opExtrude","SWEPT_EDGE",EDGE,{"disambiguationData":[OSD([sQuery(id+"F1.wireOp",EDGE,"E17"),sQuery(id+"F1.wireOp",EDGE,"E18")])]}),makeQuery(id+"F4.opExtrude","SWEPT_EDGE",EDGE,{"disambiguationData":[OSD([sQuery(id+"F3.wireOp",EDGE,"E75.0"),sQuery(id+"F3.wireOp",EDGE,"E93.0")])]})]});
            fillet(context, id + "F12", {"entities" : qUnion([Q0, Q1, Q2, Q3, Q4, Q5, Q6, Q7, Q8, Q9, Q10, Q11, Q12, Q13, Q14, Q15, Q16, Q17, Q18, Q19, Q20, Q21, Q22, Q23, Q24, Q25, Q26, Q27, Q28, Q29, Q30, Q31, Q32, Q33, Q34, Q35, Q36, Q37, Q38, Q39, Q40, Q41, Q42, Q43, Q44, Q45, Q46, Q47, Q48, Q49, Q50, Q51]), "radius" : 1 * mm, "tangentPropagation" : true, "allowEdgeOverflow" : false});
        }
        {
            var Q0;
            Q0=makeQuery(id+"F2.opExtrude","SWEPT_EDGE",EDGE,{"disambiguationData":[OSD([sQuery(id+"F1.wireOp",EDGE,"E13.0.2"),sQuery(id+"F1.wireOp",EDGE,"E43")])]});
            var Q1;
            Q1=makeQuery(id+"F2.opExtrude","SWEPT_EDGE",EDGE,{"disambiguationData":[OSD([sQuery(id+"F1.wireOp",EDGE,"E13.0.0"),sQuery(id+"F1.wireOp",EDGE,"E45")])]});
            fillet(context, id + "F13", {"entities" : qUnion([Q0, Q1]), "radius" : .5 * mm, "tangentPropagation" : true, "allowEdgeOverflow" : false});
        }
    });
